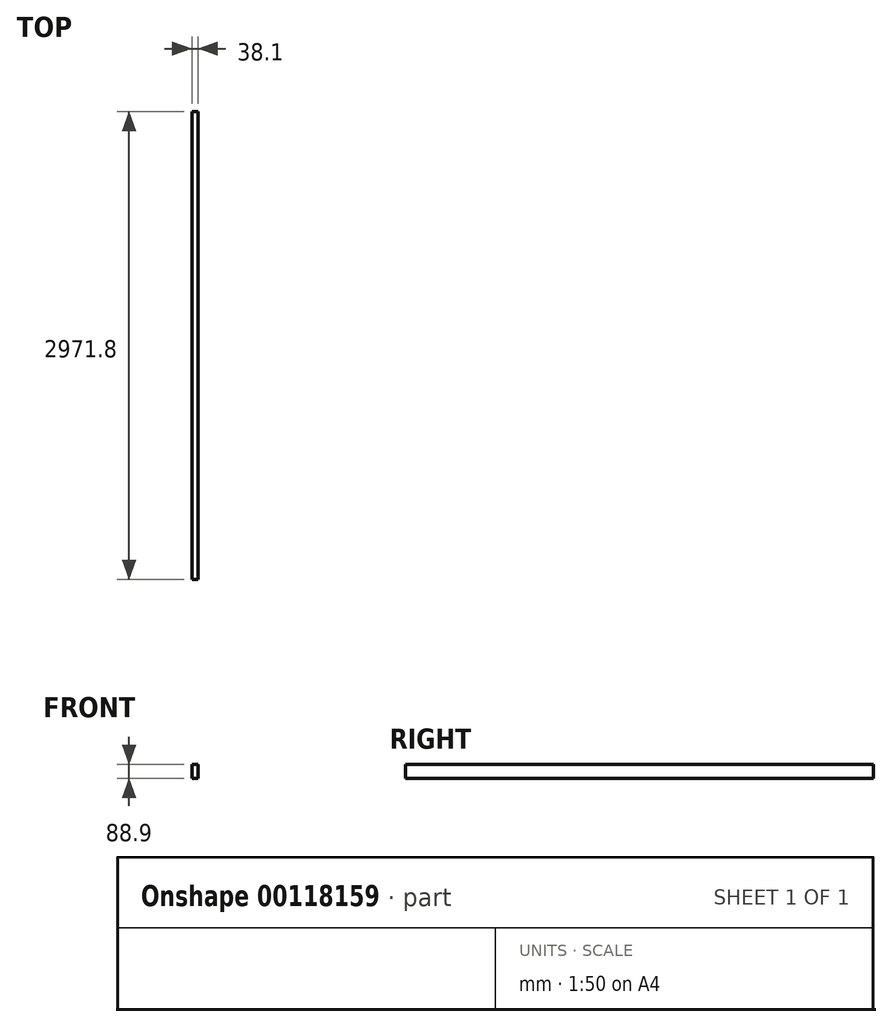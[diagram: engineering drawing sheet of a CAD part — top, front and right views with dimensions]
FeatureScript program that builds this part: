
annotation { "Feature Type Name" : "Feature", "Feature Type Description" : "" }
export const myFeature = defineFeature(function(context is Context, id is Id, definition is map)
    precondition{}
    {
        {
            var Q0;
            Q0=qCreatedBy(makeId("Front.planeOp"),FACE);
            var sketch = newSketch(context, id + "F0", { "sketchPlane" : qUnion([Q0])});
            skLineSegment(sketch, "E0.bottom", {"start": v(0, 0) * mm, "end": v(38.1, 0) * mm});
            skLineSegment(sketch, "E0.top", {"start": v(0, 88.9) * mm, "end": v(38.1, 88.9) * mm});
            skLineSegment(sketch, "E0.left", {"start": v(0, 0) * mm, "end": v(0, 88.9) * mm});
            skLineSegment(sketch, "E0.right", {"start": v(38.1, 0) * mm, "end": v(38.1, 88.9) * mm});
            skSolve(sketch);
        }
        {
            var Q0;
            Q0 = qSketchRegion(id + "F0", true);
            extrude(context, id + "F1", {"entities" : qUnion([Q0]), "depth" : 2971.8 * mm});
        }
    });
